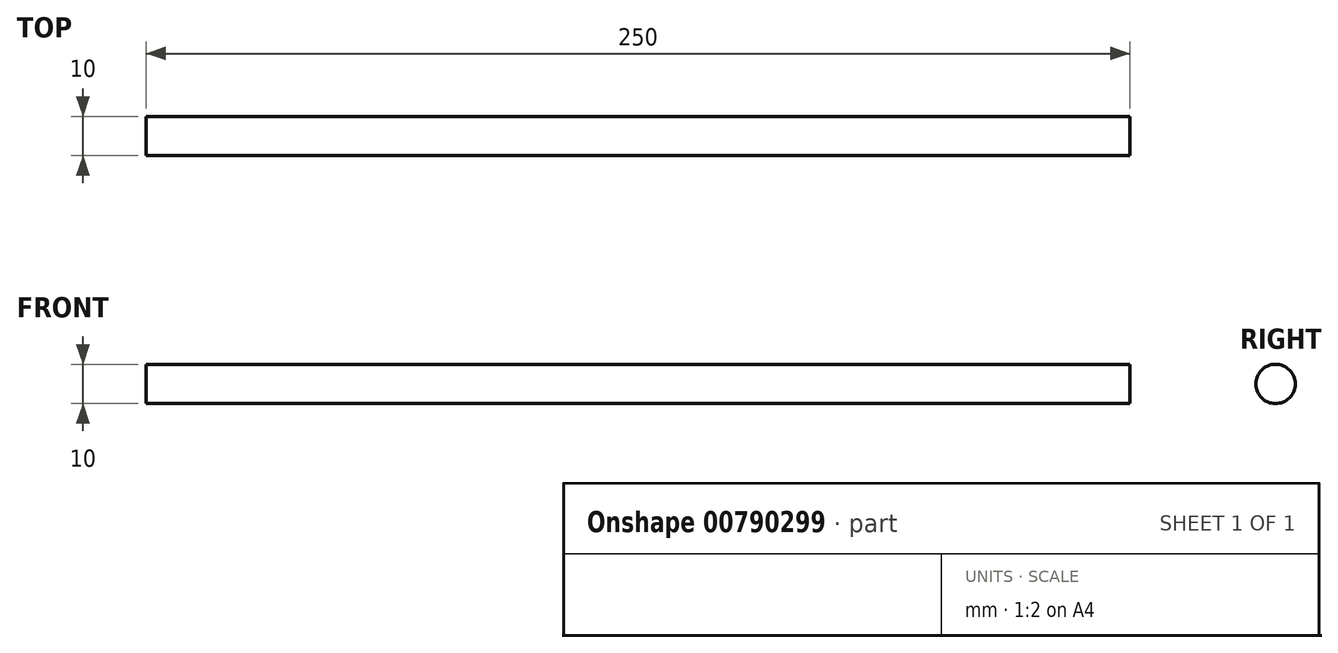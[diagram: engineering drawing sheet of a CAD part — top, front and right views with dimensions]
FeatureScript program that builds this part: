
annotation { "Feature Type Name" : "Feature", "Feature Type Description" : "" }
export const myFeature = defineFeature(function(context is Context, id is Id, definition is map)
    precondition{}
    {
        {
            var Q0;
            Q0=qCreatedBy(makeId("Right.planeOp"),FACE);
            var sketch = newSketch(context, id + "F0", { "sketchPlane" : qUnion([Q0])});
            skCircle(sketch, "E0", {"center": v(0, 0) * mm, "radius": 5 * mm});
            skSolve(sketch);
        }
        {
            var Q0;
            Q0 = qSketchRegion(id + "F0", true);
            extrude(context, id + "F1", {"entities" : qUnion([Q0]), "depth" : 250 * mm, "offsetDistance" : 25 * mm});
        }
    });
